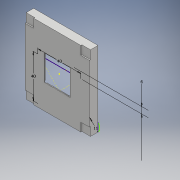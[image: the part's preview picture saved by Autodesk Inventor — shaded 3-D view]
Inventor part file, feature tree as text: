
AUTODESK INVENTOR PART (.ipt)
format: ipt  version: 2018 (Build 220112000, 112)  size: 173,056 bytes
history: native  units: mm
features: sketch x9, extrude x5
ambient origin geometry x8: Origin, YZ Plane, XZ Plane, XY Plane, X Axis, Y Axis, Z Axis, Center Point
bodies: Solid1 (feature_tree)
feature tree (14):
  extrude  "Extrusion1"  Depth=70.0mm
  extrude  "Extrusion2"  Depth=64.0mm
  extrude  "Extrusion3"  Depth=6.0mm TaperAngle=0.0deg
  extrude  "Extrusion4"  Depth=24.0mm
  sketch  "Sketch5"  dims[d10=26.0mm d11=26.0mm]
  sketch  "Sketch6"  dims[d16=1.5mm d17=0.0mm]
  sketch  "Sketch7"  dims[d18=24.0mm]
  extrude  "Extrusion5"  Depth=26.0mm
  sketch  "Sketch9"  dims[d20=1.5mm d21=0.0mm d23=3.0mm d24=3.0mm d25=3.0mm d26=3.0mm d27=40.0mm d28=40.0mm d29=6.0mm d30=8.0mm d31=8.0mm d32=8.0mm d33=8.0mm d34=8.0mm d35=8.0mm d36=8.0mm d37=8.0mm d38=1.0mm d39=0.0mm d40=11.0mm]
  sketch  "Sketch1"  dims[d0=60.0mm d1=70.0mm]
  sketch  "Sketch2"  dims[d2=8.0mm d3=0.0mm d4=64.0mm]
  sketch  "Sketch3"  dims[d5=54.0mm d6=6.0mm d7=0.0mm]
  sketch  "Sketch4"  dims[d8=24.0mm d9=24.0mm]
  sketch  "Sketch8"  dims[d19=24.0mm]
